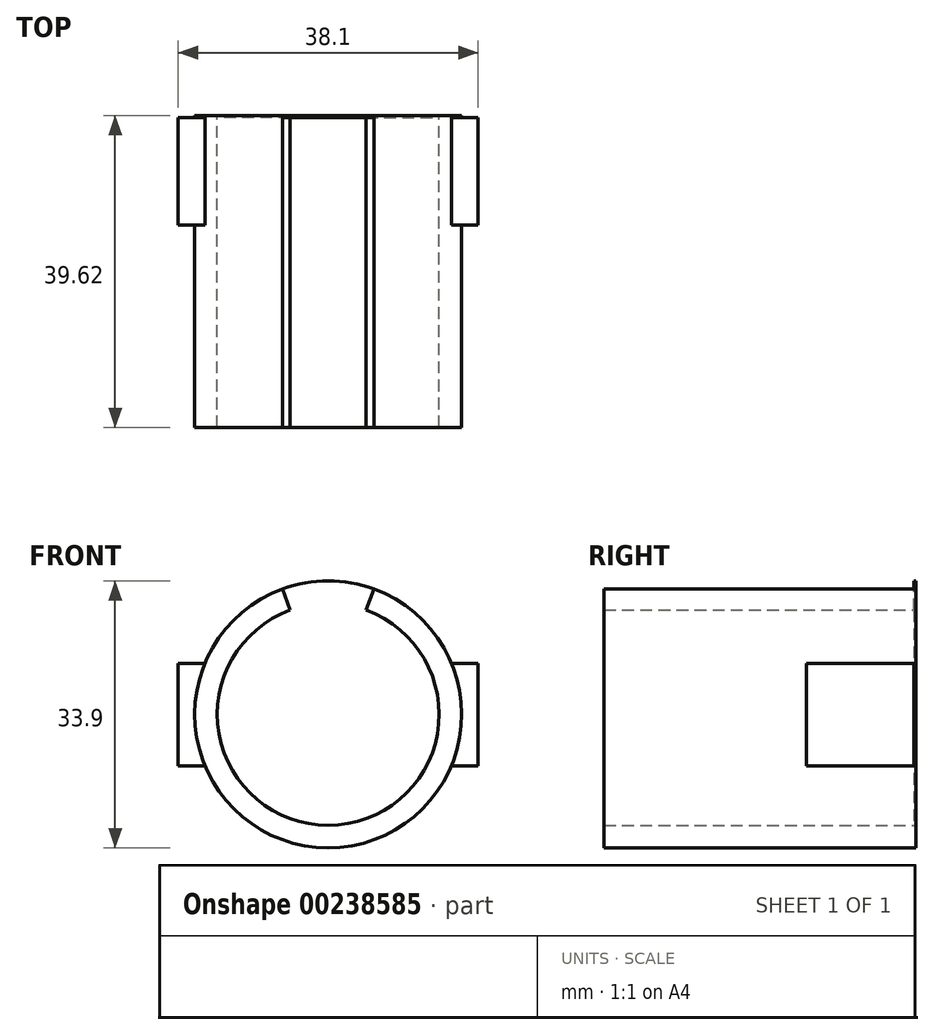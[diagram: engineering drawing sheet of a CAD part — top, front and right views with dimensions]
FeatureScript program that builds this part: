
annotation { "Feature Type Name" : "Feature", "Feature Type Description" : "" }
export const myFeature = defineFeature(function(context is Context, id is Id, definition is map)
    precondition{}
    {
        {
            assignVariable(context, id + "F0", {"name" : "length", "anyValue" : 609.6 * mm});
        }
        {
            assignVariable(context, id + "F1", {"name" : "gripLength", "anyValue" : getVariable(context, 'length') / 16});
        }
        {
            assignVariable(context, id + "F2", {"name" : "tolerance", "anyValue" : 0.03});
        }
        {
            assignVariable(context, id + "F3", {"name" : "motorLength", "anyValue" : 39.37 * mm});
        }
        {
            var Q0;
            Q0=qCreatedBy(makeId("Front.planeOp"),FACE);
            var sketch = newSketch(context, id + "F4", { "sketchPlane" : qUnion([Q0])});
            skCircle(sketch, "E0", {"center": v(0, 0) * mm, "radius": 14.1 * mm});
            skCircle(sketch, "E1", {"center": v(0, 0) * mm, "radius": 16.95 * mm});
            skLineSegment(sketch, "E2", {"start": v(0, 0) * mm, "end": v(5.8, 15.93) * mm});
            skLineSegment(sketch, "E3", {"start": v(0, 0) * mm, "end": v(-5.8, 15.93) * mm});
            skLineSegment(sketch, "E4", {"start": v(0, 0) * mm, "end": v(14.1, 0) * mm});
            skLineSegment(sketch, "E5", {"start": v(0, 0) * mm, "end": v(-14.1, 0) * mm});
            skSolve(sketch);
        }
        {
            var Q0;
            Q0 = qSketchRegion(id + "F4", true);
            extrude(context, id + "F5", {"entities" : qUnion([Q0]), "depth" : getVariable(context, 'motorLength'), "offsetDistance" : 25.4 * mm});
        }
        {
            var Q0;
            Q0=qCreatedBy(makeId("Right.planeOp"),FACE);
            var sketch = newSketch(context, id + "F6", { "sketchPlane" : qUnion([Q0])});
            skLineSegment(sketch, "E6", {"start": v(0, 0) * mm, "end": v(0, 6.5) * mm});
            skLineSegment(sketch, "E7", {"start": v(0, 6.5) * mm, "end": v(-13.65, 6.5) * mm});
            skLineSegment(sketch, "E8", {"start": v(0, 0) * mm, "end": v(0, -6.5) * mm});
            skLineSegment(sketch, "E9", {"start": v(0, -6.5) * mm, "end": v(-13.65, -6.5) * mm});
            skLineSegment(sketch, "E10", {"start": v(-13.65, -6.5) * mm, "end": v(-13.65, 6.5) * mm});
            skSolve(sketch);
        }
        {
            var Q0;
            Q0 = qSketchRegion(id + "F6", true);
            extrude(context, id + "F7", {"entities" : qUnion([Q0]), "operationType" : NewBodyOperationType.ADD, "endBound" : BoundingType.SYMMETRIC, "depth" : getVariable(context, 'gripLength'), "offsetDistance" : 25.4 * mm});
        }
        {
            var Q0;
            {var subQ0=sQuery(id+"F4.wireOp",EDGE,"E4");Q0=makeQuery(id+"F4.imprint","IMPRINT",FACE,{"disambiguationData":[TD([[makeQuery(id+"F4.imprint","IMPRINT",EDGE,{"derivedFrom":subQ0}),-1.0]])]});}
            var Q1;
            {var subQ0=sQuery(id+"F4.wireOp",EDGE,"E5");Q1=makeQuery(id+"F4.imprint","IMPRINT",FACE,{"disambiguationData":[TD([[makeQuery(id+"F4.imprint","IMPRINT",EDGE,{"derivedFrom":subQ0}),-1.0]])]});}
            var Q2;
            {var subQ0=sQuery(id+"F4.wireOp",EDGE,"E4");Q2=makeQuery(id+"F4.imprint","IMPRINT",FACE,{"disambiguationData":[TD([[makeQuery(id+"F4.imprint","IMPRINT",EDGE,{"derivedFrom":subQ0}),1.0]])]});}
            var Q3;
            {var subQ0=sQuery(id+"F4.wireOp",EDGE,"E2");var subQ1=sQuery(id+"F4.wireOp",EDGE,"E0");var subQ2=makeQuery(id+"F4.imprint","INTERSECT",VERTEX,{"derivedFrom":[subQ1,subQ0]});Q3=makeQuery(id+"F4.imprint","IMPRINT",FACE,{"disambiguationData":[TD([[makeQuery(id+"F4.imprint","IMPRINT",EDGE,{"disambiguationData":[TD([[subQ2,-1.0]])],"derivedFrom":subQ1}),1.0]])]});}
            var Q4;
            {var subQ0=sQuery(id+"F4.wireOp",EDGE,"E2");var subQ1=sQuery(id+"F4.wireOp",EDGE,"E0");var subQ2=makeQuery(id+"F4.imprint","INTERSECT",VERTEX,{"derivedFrom":[subQ1,subQ0]});Q4=makeQuery(id+"F4.imprint","IMPRINT",FACE,{"disambiguationData":[TD([[makeQuery(id+"F4.imprint","IMPRINT",EDGE,{"disambiguationData":[TD([[subQ2,-1.0]])],"derivedFrom":subQ1}),-1.0]])]});}
            extrude(context, id + "F8", {"entities" : qUnion([Q0, Q1, Q2, Q3, Q4]), "operationType" : NewBodyOperationType.REMOVE, "depth" : getVariable(context, 'motorLength'), "offsetDistance" : 25.4 * mm});
        }
        {
            var Q0;
            {var subQ0=sQuery(id+"F4.wireOp",EDGE,"E0");var subQ1=makeQuery(id+"F4.imprint","INTERSECT",VERTEX,{"derivedFrom":[subQ0,sQuery(id+"F4.wireOp",EDGE,"E4")]});Q0=makeQuery(id+"F4.imprint","IMPRINT",FACE,{"disambiguationData":[TD([[makeQuery(id+"F4.imprint","IMPRINT",EDGE,{"disambiguationData":[TD([[subQ1,-1.0]])],"derivedFrom":subQ0}),-1.0]])]});}
            var Q1;
            {var subQ0=sQuery(id+"F4.wireOp",EDGE,"E2");var subQ1=sQuery(id+"F4.wireOp",EDGE,"E0");var subQ2=makeQuery(id+"F4.imprint","INTERSECT",VERTEX,{"derivedFrom":[subQ1,subQ0]});Q1=makeQuery(id+"F4.imprint","IMPRINT",FACE,{"disambiguationData":[TD([[makeQuery(id+"F4.imprint","IMPRINT",EDGE,{"disambiguationData":[TD([[subQ2,-1.0]])],"derivedFrom":subQ1}),-1.0]])]});}
            var Q2;
            {var subQ0=sQuery(id+"F4.wireOp",EDGE,"E5");Q2=makeQuery(id+"F4.imprint","IMPRINT",FACE,{"disambiguationData":[TD([[makeQuery(id+"F4.imprint","IMPRINT",EDGE,{"derivedFrom":subQ0}),-1.0]])]});}
            var Q3;
            {var subQ0=sQuery(id+"F4.wireOp",EDGE,"E4");Q3=makeQuery(id+"F4.imprint","IMPRINT",FACE,{"disambiguationData":[TD([[makeQuery(id+"F4.imprint","IMPRINT",EDGE,{"derivedFrom":subQ0}),-1.0]])]});}
            var Q4;
            {var subQ0=sQuery(id+"F4.wireOp",EDGE,"E4");Q4=makeQuery(id+"F4.imprint","IMPRINT",FACE,{"disambiguationData":[TD([[makeQuery(id+"F4.imprint","IMPRINT",EDGE,{"derivedFrom":subQ0}),1.0]])]});}
            var Q5;
            {var subQ0=sQuery(id+"F4.wireOp",EDGE,"E2");var subQ1=sQuery(id+"F4.wireOp",EDGE,"E0");var subQ2=makeQuery(id+"F4.imprint","INTERSECT",VERTEX,{"derivedFrom":[subQ1,subQ0]});Q5=makeQuery(id+"F4.imprint","IMPRINT",FACE,{"disambiguationData":[TD([[makeQuery(id+"F4.imprint","IMPRINT",EDGE,{"disambiguationData":[TD([[subQ2,-1.0]])],"derivedFrom":subQ1}),1.0]])]});}
            extrude(context, id + "F9", {"entities" : qUnion([Q0, Q1, Q2, Q3, Q4, Q5]), "operationType" : NewBodyOperationType.ADD, "oppositeDirection" : true, "depth" : (getVariable(context, 'tolerance') * 10) * mm, "offsetDistance" : 25.4 * mm});
        }
    });
